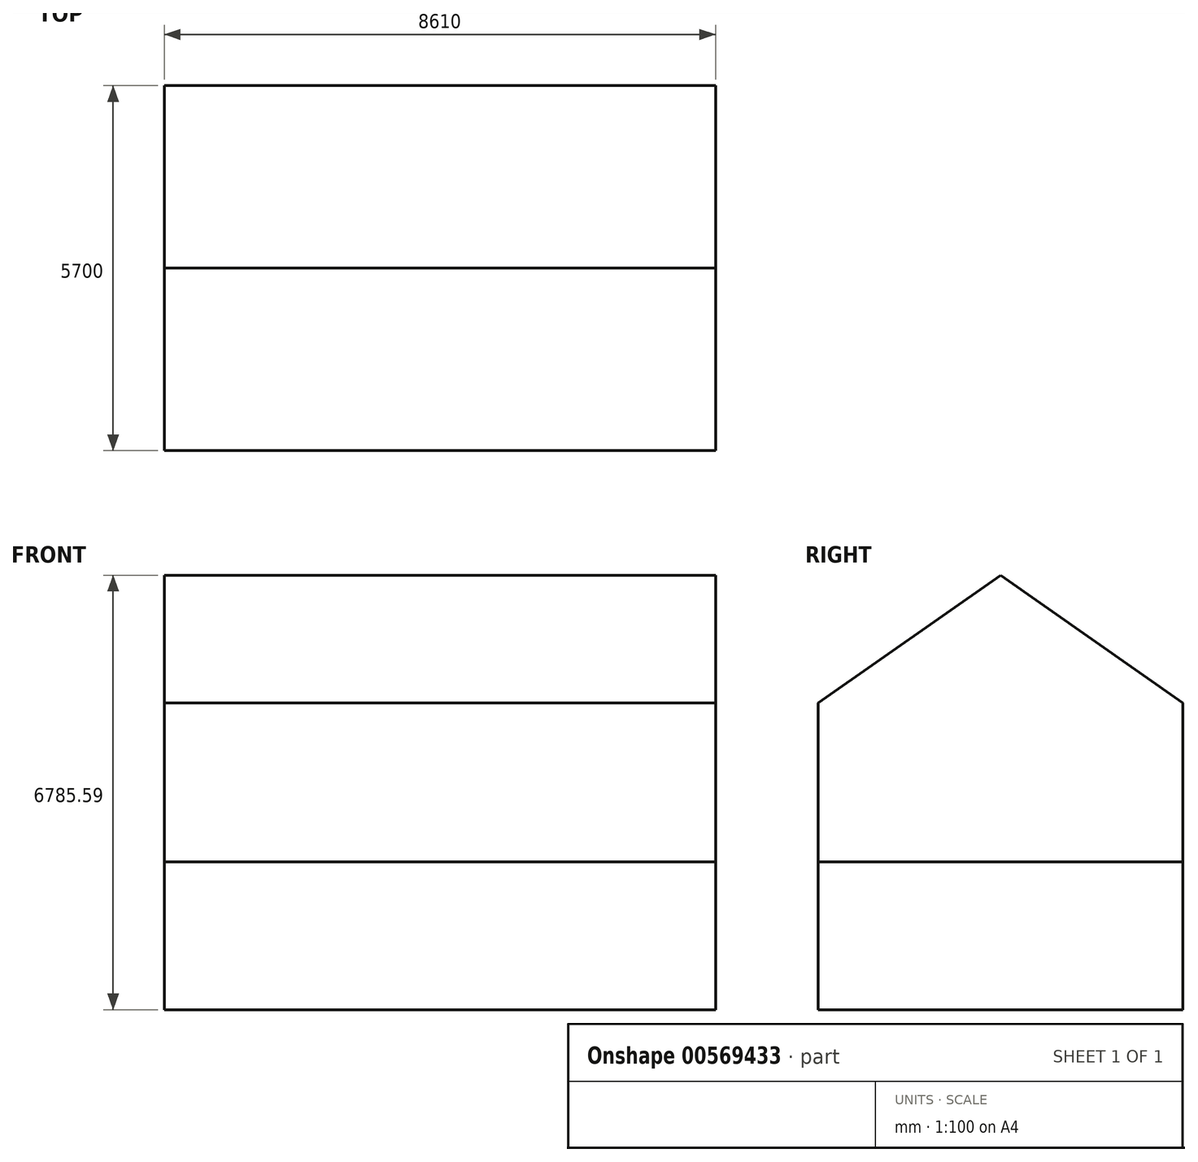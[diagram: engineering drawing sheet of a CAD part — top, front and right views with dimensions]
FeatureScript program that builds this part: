
annotation { "Feature Type Name" : "Feature", "Feature Type Description" : "" }
export const myFeature = defineFeature(function(context is Context, id is Id, definition is map)
    precondition{}
    {
        {
            var Q0;
            Q0=qCreatedBy(makeId("Right.planeOp"),FACE);
            var sketch = newSketch(context, id + "F0", { "sketchPlane" : qUnion([Q0])});
            skLineSegment(sketch, "E0", {"start": v(0, 4475.6) * mm, "end": v(-2850, 2480) * mm});
            skLineSegment(sketch, "E1", {"start": v(-2850, 2480) * mm, "end": v(-2850, 0) * mm});
            skLineSegment(sketch, "E2.MirrorCS", {"start": v(0, 4475.6) * mm, "end": v(2850, 2480) * mm});
            skLineSegment(sketch, "E3.MirrorCS", {"start": v(2850, 2480) * mm, "end": v(2850, 0) * mm});
            skLineSegment(sketch, "E4", {"start": v(-2850, 0) * mm, "end": v(2850, 0) * mm});
            skSolve(sketch);
        }
        {
            var Q0;
            Q0 = qSketchRegion(id + "F0", true);
            extrude(context, id + "F1", {"entities" : qUnion([Q0]), "oppositeDirection" : true, "depth" : 8610 * mm, "offsetDistance" : 25 * mm});
        }
        {
            var Q0;
            Q0=makeQuery(id+"F1.opExtrude","SWEPT_FACE",FACE,{"disambiguationData":[OSD([sQuery(id+"F0.wireOp",EDGE,"E4")])]});
            extrude(context, id + "F2", {"entities" : qUnion([Q0]), "depth" : 2310 * mm, "offsetDistance" : 25 * mm});
        }
    });
